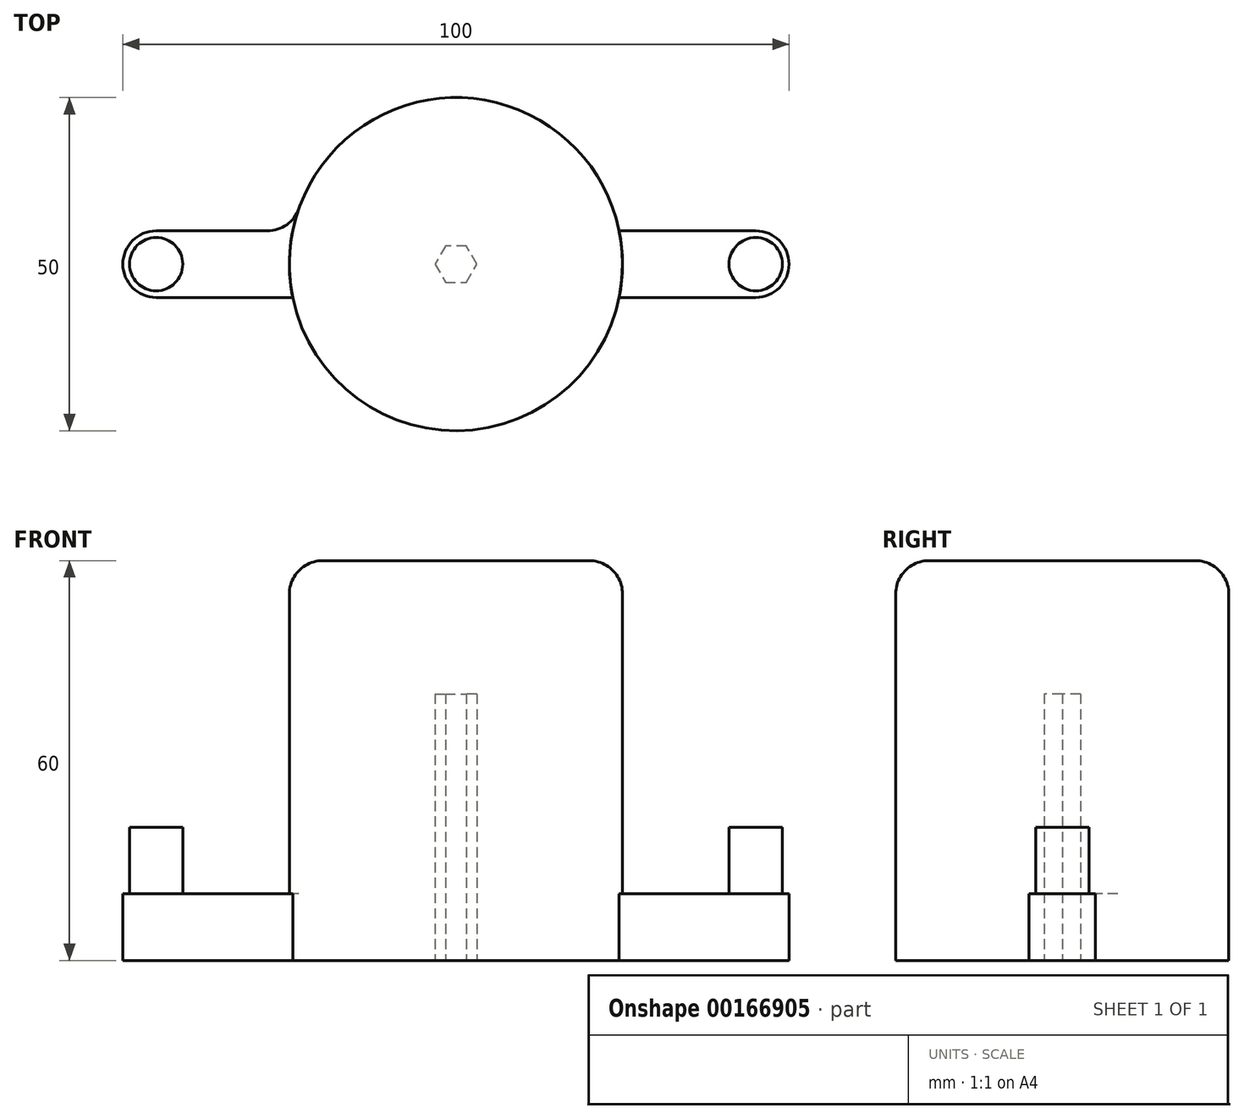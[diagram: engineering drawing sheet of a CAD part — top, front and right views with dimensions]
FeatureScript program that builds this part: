
annotation { "Feature Type Name" : "Feature", "Feature Type Description" : "" }
export const myFeature = defineFeature(function(context is Context, id is Id, definition is map)
    precondition{}
    {
        {
            var Q0;
            Q0=qCreatedBy(makeId("Top.planeOp"),FACE);
            var sketch = newSketch(context, id + "F0", { "sketchPlane" : qUnion([Q0])});
            skCircle(sketch, "E0", {"center": v(0, 0) * mm, "radius": 25 * mm});
            skSolve(sketch);
        }
        {
            var Q0;
            Q0 = qSketchRegion(id + "F0", true);
            extrude(context, id + "F1", {"entities" : qUnion([Q0]), "depth" : 50 * mm});
        }
        {
            var Q0;
            Q0=makeQuery(id+"F1.opExtrude","CAP_EDGE",EDGE,{"disambiguationData":[OSD([sQuery(id+"F0.wireOp",EDGE,"E0")])],"isStart":false});
            fillet(context, id + "F2", {"entities" : qUnion([Q0]), "radius" : 5 * mm, "tangentPropagation" : true, "allowEdgeOverflow" : false});
        }
        {
            var Q0;
            Q0=makeQuery(id+"F1.opExtrude","CAP_FACE",FACE,{"disambiguationData":[OSD([sQuery(id+"F0.wireOp",EDGE,"E0")])],"isStart":true});
            var sketch = newSketch(context, id + "F3", { "sketchPlane" : qUnion([Q0])});
            skLineSegment(sketch, "E1.bottom", {"start": v(-50, 5) * mm, "end": v(50, 5) * mm});
            skLineSegment(sketch, "E1.top", {"start": v(-50, -5) * mm, "end": v(50, -5) * mm});
            skLineSegment(sketch, "E1.left", {"start": v(-50, 5) * mm, "end": v(-50, -5) * mm});
            skLineSegment(sketch, "E1.right", {"start": v(50, 5) * mm, "end": v(50, -5) * mm});
            skSolve(sketch);
        }
        {
            var Q0;
            Q0 = qSketchRegion(id + "F3", true);
            extrude(context, id + "F4", {"entities" : qUnion([Q0]), "operationType" : NewBodyOperationType.ADD, "depth" : 10 * mm});
        }
        {
            var Q0;
            Q0=makeQuery(id+"F4.opExtrude","SWEPT_EDGE",EDGE,{"disambiguationData":[OSD([sQuery(id+"F3.wireOp",EDGE,"E1.top"),sQuery(id+"F3.wireOp",EDGE,"E1.left")])]});
            var Q1;
            Q1=makeQuery(id+"F4.opExtrude","SWEPT_EDGE",EDGE,{"disambiguationData":[OSD([sQuery(id+"F3.wireOp",EDGE,"E1.bottom"),sQuery(id+"F3.wireOp",EDGE,"E1.left")])]});
            var Q2;
            Q2=makeQuery(id+"F4.opExtrude","SWEPT_EDGE",EDGE,{"disambiguationData":[OSD([sQuery(id+"F3.wireOp",EDGE,"E1.bottom"),sQuery(id+"F3.wireOp",EDGE,"E1.right")])]});
            var Q3;
            Q3=makeQuery(id+"F4.opExtrude","SWEPT_EDGE",EDGE,{"disambiguationData":[OSD([sQuery(id+"F3.wireOp",EDGE,"E1.top"),sQuery(id+"F3.wireOp",EDGE,"E1.right")])]});
            fillet(context, id + "F5", {"entities" : qUnion([Q0, Q1, Q2, Q3]), "radius" : 5 * mm, "tangentPropagation" : true, "allowEdgeOverflow" : false});
        }
        {
            var Q0;
            {var subQ0=sQuery(id+"F3.wireOp",EDGE,"E1.top");var subQ1=sQuery(id+"F3.wireOp",EDGE,"E1.bottom");var subQ3=sQuery(id+"F3.wireOp",EDGE,"E1.left");Q0=makeQuery(id+"F4.boolean.opBoolean","SPLIT",FACE,{"disambiguationData":[TD([makeQuery(id+"F4.opExtrude","SWEPT_FACE",FACE,{"disambiguationData":[OSD([subQ3])]})])],"derivedFrom":makeQuery(id+"F4.opExtrude","CAP_FACE",FACE,{"disambiguationData":[OSD([subQ1,subQ0,subQ3,sQuery(id+"F3.wireOp",EDGE,"E1.right")])],"isStart":true})});}
            var sketch = newSketch(context, id + "F6", { "sketchPlane" : qUnion([Q0])});
            skPoint(sketch, "E2", {"position": v(-45, 0) * mm});
            skPoint(sketch, "E3", {"position": v(45, 0) * mm});
            skCircle(sketch, "E4", {"center": v(-45, 0) * mm, "radius": 4 * mm});
            skCircle(sketch, "E5", {"center": v(45, 0) * mm, "radius": 4 * mm});
            skSolve(sketch);
        }
        {
            var Q0;
            Q0 = qSketchRegion(id + "F6", true);
            extrude(context, id + "F7", {"entities" : qUnion([Q0]), "operationType" : NewBodyOperationType.ADD, "depth" : 10 * mm});
        }
        {
            var Q0;
            {var subQ0=sQuery(id+"F0.wireOp",EDGE,"E0");var subQ1=sQuery(id+"F3.wireOp",EDGE,"E1.bottom");Q0=makeQuery(id+"F4.boolean.opBoolean","SPLIT",FACE,{"disambiguationData":[TD([makeQuery(id+"F4.opExtrude","SWEPT_FACE",FACE,{"disambiguationData":[OSD([subQ1])]})])],"derivedFrom":makeQuery(id+"F1.opExtrude","CAP_FACE",FACE,{"disambiguationData":[OSD([subQ0])],"isStart":true})});}
            var Q1;
            {var subQ0=sQuery(id+"F0.wireOp",EDGE,"E0");var subQ1=sQuery(id+"F3.wireOp",EDGE,"E1.top");Q1=makeQuery(id+"F4.boolean.opBoolean","SPLIT",FACE,{"disambiguationData":[TD([makeQuery(id+"F4.opExtrude","SWEPT_FACE",FACE,{"disambiguationData":[OSD([subQ1])]})])],"derivedFrom":makeQuery(id+"F1.opExtrude","CAP_FACE",FACE,{"disambiguationData":[OSD([subQ0])],"isStart":true})});}
            extrude(context, id + "F8", {"entities" : qUnion([Q0, Q1]), "operationType" : NewBodyOperationType.ADD, "depth" : 10 * mm});
        }
        {
            var Q0;
            {var subQ0=sQuery(id+"F0.wireOp",EDGE,"E0");var subQ2=sQuery(id+"F3.wireOp",EDGE,"E1.right");var subQ3=sQuery(id+"F3.wireOp",EDGE,"E1.left");var subQ4=sQuery(id+"F3.wireOp",EDGE,"E1.top");var subQ5=sQuery(id+"F3.wireOp",EDGE,"E1.bottom");var subQ7=makeQuery(id+"F1.opExtrude","CAP_FACE",FACE,{"disambiguationData":[OSD([subQ0])],"isStart":true});Q0=makeQuery(id+"F8.boolean.opBoolean","MERGE",FACE,{"derivedFrom":[makeQuery(id+"F4.opExtrude","CAP_FACE",FACE,{"disambiguationData":[OSD([subQ5,subQ4,subQ3,subQ2])],"isStart":false}),makeQuery(id+"F8.opExtrude","CAP_FACE",FACE,{"disambiguationData":[OSD([subQ0]),TDD([makeQuery(id+"F4.boolean.opBoolean","SPLIT",FACE,{"disambiguationData":[TD([makeQuery(id+"F4.opExtrude","SWEPT_FACE",FACE,{"disambiguationData":[OSD([subQ5])]})])],"derivedFrom":subQ7})])],"isStart":false}),makeQuery(id+"F8.opExtrude","CAP_FACE",FACE,{"disambiguationData":[OSD([subQ0]),TDD([makeQuery(id+"F4.boolean.opBoolean","SPLIT",FACE,{"disambiguationData":[TD([makeQuery(id+"F4.opExtrude","SWEPT_FACE",FACE,{"disambiguationData":[OSD([subQ4])]})])],"derivedFrom":subQ7})])],"isStart":false})]});}
            var sketch = newSketch(context, id + "F9", { "sketchPlane" : qUnion([Q0])});
            skPoint(sketch, "E6", {"position": v(0, 0) * mm});
            skCircle(sketch, "E7.cCircle", {"center": v(0, 0) * mm, "radius": 2.73 * mm, "construction": true});
            skLineSegment(sketch, "E7.0", {"start": v(-1.57, 2.73) * mm, "end": v(1.57, 2.73) * mm});
            skLineSegment(sketch, "E7.1", {"start": v(1.57, 2.73) * mm, "end": v(3.15, 0) * mm});
            skLineSegment(sketch, "E7.2", {"start": v(3.15, 0) * mm, "end": v(1.58, -2.73) * mm});
            skLineSegment(sketch, "E7.3", {"start": v(1.58, -2.73) * mm, "end": v(-1.57, -2.73) * mm});
            skLineSegment(sketch, "E7.4", {"start": v(-1.57, -2.73) * mm, "end": v(-3.15, 0) * mm});
            skLineSegment(sketch, "E7.5", {"start": v(-3.15, 0) * mm, "end": v(-1.57, 2.73) * mm});
            skPoint(sketch, "E7.0.midPoint", {"position": v(0, 2.73) * mm});
            skSolve(sketch);
        }
        {
            var Q0;
            Q0=makeQuery(id+"F9.imprint","IMPRINT",FACE,{"disambiguationData":[TD([[makeQuery(id+"F9.imprint","IMPRINT",EDGE,{"derivedFrom":sQuery(id+"F9.wireOp",EDGE,"E7.0")}),-1.0]])]});
            extrude(context, id + "F10", {"entities" : qUnion([Q0]), "operationType" : NewBodyOperationType.REMOVE, "oppositeDirection" : true, "depth" : 40 * mm});
        }
        {
            var Q0;
            Q0=makeQuery(id+"F2.opFillet","BLEND_FACE",FACE,{"disambiguationData":[OSD([sQuery(id+"F0.wireOp",EDGE,"E0")])]});
            var Q1;
            {var subQ0=sQuery(id+"F3.wireOp",EDGE,"E1.top");var subQ1=sQuery(id+"F3.wireOp",EDGE,"E1.right");var subQ2=sQuery(id+"F3.wireOp",EDGE,"E1.left");var subQ3=sQuery(id+"F3.wireOp",EDGE,"E1.bottom");var subQ4=sQuery(id+"F0.wireOp",EDGE,"E0");Q1=makeQuery(id+"F8.opExtrude","SWEPT_EDGE",EDGE,{"disambiguationData":[OSD([subQ4,subQ3,subQ0,subQ2,subQ1]),TDD([makeQuery(id+"F4.boolean.opBoolean","TWEAK_VERTEX",VERTEX,{"disambiguationData":[OD(1.0)],"derivedFrom":[makeQuery(id+"F1.opExtrude","CAP_FACE",FACE,{"disambiguationData":[OSD([subQ4])],"isStart":true}),makeQuery(id+"F1.opExtrude","SWEPT_FACE",FACE,{"disambiguationData":[OSD([subQ4])]}),makeQuery(id+"F4.opExtrude","CAP_FACE",FACE,{"disambiguationData":[OSD([subQ3,subQ0,subQ2,subQ1])],"isStart":true}),makeQuery(id+"F4.opExtrude","SWEPT_FACE",FACE,{"disambiguationData":[OSD([subQ0])]})]})])]});}
            var Q2;
            {var subQ0=sQuery(id+"F3.wireOp",EDGE,"E1.right");var subQ1=sQuery(id+"F3.wireOp",EDGE,"E1.left");var subQ2=sQuery(id+"F3.wireOp",EDGE,"E1.top");var subQ3=sQuery(id+"F3.wireOp",EDGE,"E1.bottom");var subQ4=sQuery(id+"F0.wireOp",EDGE,"E0");Q2=makeQuery(id+"F8.opExtrude","SWEPT_EDGE",EDGE,{"disambiguationData":[OSD([subQ4,subQ3,subQ2,subQ1,subQ0]),TDD([makeQuery(id+"F4.boolean.opBoolean","TWEAK_VERTEX",VERTEX,{"disambiguationData":[OD(1.0)],"derivedFrom":[makeQuery(id+"F1.opExtrude","CAP_FACE",FACE,{"disambiguationData":[OSD([subQ4])],"isStart":true}),makeQuery(id+"F1.opExtrude","SWEPT_FACE",FACE,{"disambiguationData":[OSD([subQ4])]}),makeQuery(id+"F4.opExtrude","SWEPT_FACE",FACE,{"disambiguationData":[OSD([subQ3])]}),makeQuery(id+"F4.opExtrude","CAP_FACE",FACE,{"disambiguationData":[OSD([subQ3,subQ2,subQ1,subQ0])],"isStart":true})]})])]});}
            var Q3;
            {var subQ0=sQuery(id+"F3.wireOp",EDGE,"E1.right");var subQ1=sQuery(id+"F3.wireOp",EDGE,"E1.left");var subQ2=sQuery(id+"F3.wireOp",EDGE,"E1.top");var subQ3=sQuery(id+"F3.wireOp",EDGE,"E1.bottom");var subQ4=sQuery(id+"F0.wireOp",EDGE,"E0");Q3=makeQuery(id+"F8.opExtrude","SWEPT_EDGE",EDGE,{"disambiguationData":[OSD([subQ4,subQ3,subQ2,subQ1,subQ0]),TDD([makeQuery(id+"F4.boolean.opBoolean","TWEAK_VERTEX",VERTEX,{"disambiguationData":[OD(0.0)],"derivedFrom":[makeQuery(id+"F1.opExtrude","CAP_FACE",FACE,{"disambiguationData":[OSD([subQ4])],"isStart":true}),makeQuery(id+"F1.opExtrude","SWEPT_FACE",FACE,{"disambiguationData":[OSD([subQ4])]}),makeQuery(id+"F4.opExtrude","SWEPT_FACE",FACE,{"disambiguationData":[OSD([subQ3])]}),makeQuery(id+"F4.opExtrude","CAP_FACE",FACE,{"disambiguationData":[OSD([subQ3,subQ2,subQ1,subQ0])],"isStart":true})]})])]});}
            var Q4;
            {var subQ0=sQuery(id+"F3.wireOp",EDGE,"E1.top");var subQ1=sQuery(id+"F3.wireOp",EDGE,"E1.right");var subQ2=sQuery(id+"F3.wireOp",EDGE,"E1.left");var subQ3=sQuery(id+"F3.wireOp",EDGE,"E1.bottom");var subQ4=sQuery(id+"F0.wireOp",EDGE,"E0");Q4=makeQuery(id+"F8.opExtrude","SWEPT_EDGE",EDGE,{"disambiguationData":[OSD([subQ4,subQ3,subQ0,subQ2,subQ1]),TDD([makeQuery(id+"F4.boolean.opBoolean","TWEAK_VERTEX",VERTEX,{"disambiguationData":[OD(0.0)],"derivedFrom":[makeQuery(id+"F1.opExtrude","CAP_FACE",FACE,{"disambiguationData":[OSD([subQ4])],"isStart":true}),makeQuery(id+"F1.opExtrude","SWEPT_FACE",FACE,{"disambiguationData":[OSD([subQ4])]}),makeQuery(id+"F4.opExtrude","CAP_FACE",FACE,{"disambiguationData":[OSD([subQ3,subQ0,subQ2,subQ1])],"isStart":true}),makeQuery(id+"F4.opExtrude","SWEPT_FACE",FACE,{"disambiguationData":[OSD([subQ0])]})]})])]});}
            fillet(context, id + "F11", {"entities" : qUnion([Q0, Q1, Q2, Q3, Q4]), "radius" : 5 * mm, "tangentPropagation" : true, "allowEdgeOverflow" : false});
        }
    });
